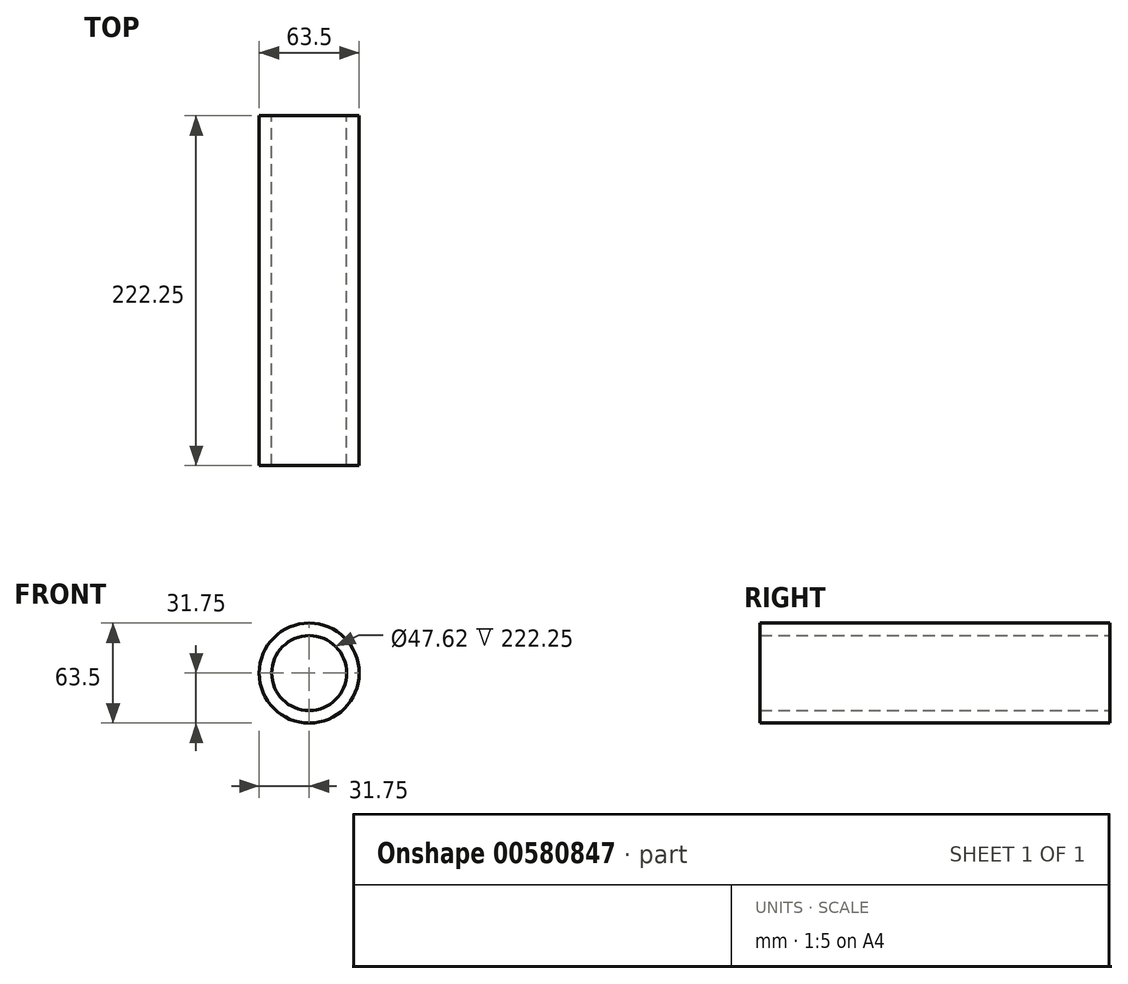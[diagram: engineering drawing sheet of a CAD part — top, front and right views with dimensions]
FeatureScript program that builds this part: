
annotation { "Feature Type Name" : "Feature", "Feature Type Description" : "" }
export const myFeature = defineFeature(function(context is Context, id is Id, definition is map)
    precondition{}
    {
        {
            var Q0;
            Q0=qCreatedBy(makeId("Front.planeOp"),FACE);
            var sketch = newSketch(context, id + "F0", { "sketchPlane" : qUnion([Q0])});
            skCircle(sketch, "E0", {"center": v(0, 0) * mm, "radius": 31.75 * mm});
            skCircle(sketch, "E1", {"center": v(0, 0) * mm, "radius": 23.81 * mm});
            skSolve(sketch);
        }
        {
            var Q0;
            Q0 = qSketchRegion(id + "F0", true);
            extrude(context, id + "F1", {"entities" : qUnion([Q0]), "depth" : 222.25 * mm, "offsetDistance" : 25.4 * mm});
        }
    });
